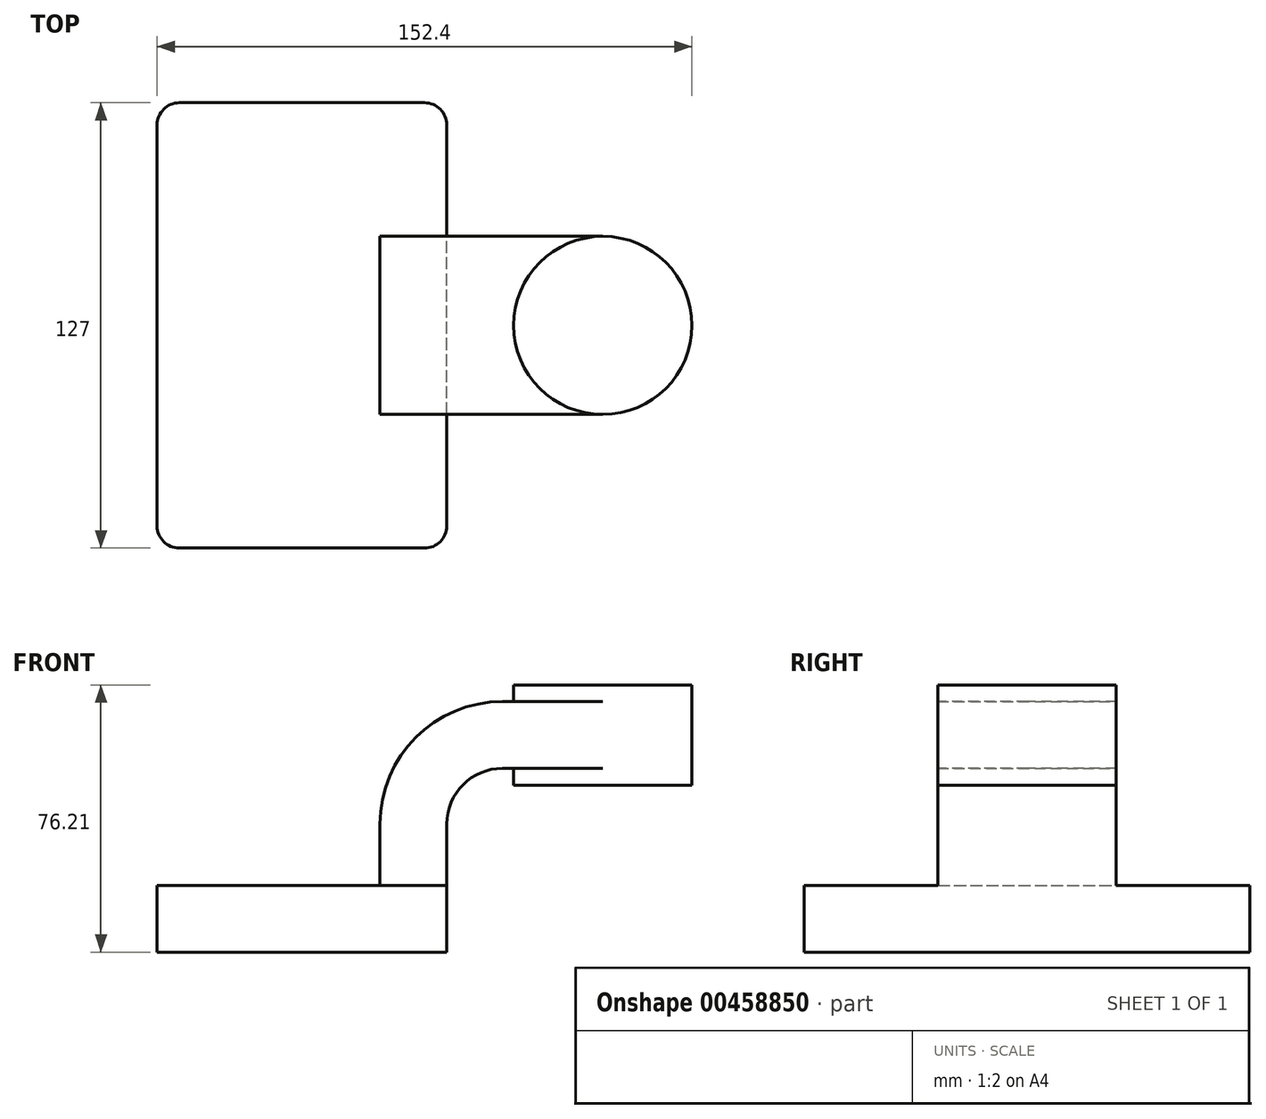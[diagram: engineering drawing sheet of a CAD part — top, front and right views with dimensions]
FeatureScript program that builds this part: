
annotation { "Feature Type Name" : "Feature", "Feature Type Description" : "" }
export const myFeature = defineFeature(function(context is Context, id is Id, definition is map)
    precondition{}
    {
        {
            var Q0;
            Q0=qCreatedBy(makeId("Front.planeOp"),FACE);
            var sketch = newSketch(context, id + "F0", { "sketchPlane" : qUnion([Q0])});
            skLineSegment(sketch, "E0.bottom", {"start": v(41.28, -9.52) * mm, "end": v(-41.28, -9.53) * mm});
            skLineSegment(sketch, "E0.top", {"start": v(41.27, 9.53) * mm, "end": v(-41.28, 9.53) * mm});
            skLineSegment(sketch, "E0.left", {"start": v(41.28, -9.52) * mm, "end": v(41.28, 9.53) * mm});
            skLineSegment(sketch, "E0.right", {"start": v(-41.28, -9.53) * mm, "end": v(-41.28, 9.53) * mm});
            skPoint(sketch, "E0.middle", {"position": v(0, 0) * mm});
            skLineSegment(sketch, "E1.bottom", {"start": v(60.33, 38.1) * mm, "end": v(111.13, 38.1) * mm});
            skLineSegment(sketch, "E1.top", {"start": v(60.32, 66.68) * mm, "end": v(111.13, 66.68) * mm});
            skLineSegment(sketch, "E1.left", {"start": v(60.33, 38.1) * mm, "end": v(60.32, 66.68) * mm});
            skLineSegment(sketch, "E1.right", {"start": v(111.13, 38.1) * mm, "end": v(111.12, 66.68) * mm});
            skPoint(sketch, "E1.middle", {"position": v(85.72, 52.39) * mm});
            skLineSegment(sketch, "E2", {"start": v(41.27, 9.53) * mm, "end": v(41.27, 27) * mm});
            skArc(sketch, "E3", {"start": v(41.27, 27) * mm, "mid": v(45.92, 38.23) * mm, "end": v(57.15, 42.88) * mm});
            skLineSegment(sketch, "E4", {"start": v(57.15, 42.88) * mm, "end": v(85.73, 42.88) * mm});
            skPoint(sketch, "E5.endSnap0", {"position": v(85.73, 66.68) * mm});
            skLineSegment(sketch, "E6.0", {"start": v(57.15, 61.93) * mm, "end": v(85.76, 61.93) * mm});
            skArc(sketch, "E6.1", {"start": v(22.23, 27) * mm, "mid": v(32.45, 51.7) * mm, "end": v(57.15, 61.93) * mm});
            skLineSegment(sketch, "E6.2", {"start": v(22.22, 9.53) * mm, "end": v(22.22, 27) * mm});
            skLineSegment(sketch, "E7", {"start": v(85.73, 38.1) * mm, "end": v(85.73, 66.68) * mm});
            skFitSpline(sketch, "E8", {"points": [v(-41.28, 9.52) * mm, v(57.15, 61.93) * mm], "startDerivative": vector(40.9, 81.24) * mm, "endDerivative": vector(129.26, -13.52) * mm});
            skSolve(sketch);
        }
        {
            var Q0;
            Q0=makeQuery(id+"F0.imprint","IMPRINT",FACE,{"disambiguationData":[TD([[makeQuery(id+"F0.imprint","IMPRINT",EDGE,{"derivedFrom":sQuery(id+"F0.wireOp",EDGE,"E0.bottom")}),-1.0]])]});
            extrude(context, id + "F1", {"entities" : qUnion([Q0]), "depth" : 127 * mm, "symmetric" : true});
        }
        {
            var Q0;
            {var subQ1=sQuery(id+"F0.wireOp",EDGE,"E2");Q0=makeQuery(id+"F0.imprint","IMPRINT",FACE,{"disambiguationData":[TD([[makeQuery(id+"F0.imprint","IMPRINT",EDGE,{"derivedFrom":subQ1}),1.0]])]});}
            var Q1;
            {var subQ0=sQuery(id+"F0.wireOp",EDGE,"E4");var subQ1=sQuery(id+"F0.wireOp",EDGE,"E1.left");var subQ2=makeQuery(id+"F0.imprint","INTERSECT",VERTEX,{"derivedFrom":[subQ1,subQ0]});Q1=makeQuery(id+"F0.imprint","IMPRINT",FACE,{"disambiguationData":[TD([[makeQuery(id+"F0.imprint","IMPRINT",EDGE,{"disambiguationData":[TD([[subQ2,-1.0]])],"derivedFrom":subQ1}),-1.0]])]});}
            extrude(context, id + "F2", {"entities" : qUnion([Q0, Q1]), "operationType" : NewBodyOperationType.ADD, "depth" : 50.8 * mm, "symmetric" : true});
        }
        {
            var Q0;
            {var subQ0=sQuery(id+"F0.wireOp",EDGE,"E1.right");Q0=makeQuery(id+"F0.imprint","IMPRINT",FACE,{"disambiguationData":[TD([[makeQuery(id+"F0.imprint","IMPRINT",EDGE,{"derivedFrom":subQ0}),1.0]])]});}
            var Q1;
            Q1=sQuery(id+"F0.wireOp",EDGE,"E7");
            revolve(context, id + "F3", {"operationType" : NewBodyOperationType.ADD, "entities" : qUnion([Q0]), "axis" : qUnion([Q1]), "revolveType" : RevolveType.FULL});
        }
        {
            var Q0;
            Q0=makeQuery(id+"F0.imprint","IMPRINT",FACE,{"disambiguationData":[TD([[makeQuery(id+"F0.imprint","IMPRINT",EDGE,{"derivedFrom":sQuery(id+"F0.wireOp",EDGE,"E6.1")}),1.0]])]});
            extrude(context, id + "F4", {"entities" : qUnion([Q0]), "operationType" : NewBodyOperationType.ADD, "depth" : 15.88 * mm, "symmetric" : true});
        }
        {
            var Q0;
            Q0=makeQuery(id+"F1.opExtrude","CAP_EDGE",EDGE,{"disambiguationData":[OSD([sQuery(id+"F0.wireOp",EDGE,"E0.right")])],"isStart":true});
            var Q1;
            Q1=makeQuery(id+"F1.opExtrude","CAP_EDGE",EDGE,{"disambiguationData":[OSD([sQuery(id+"F0.wireOp",EDGE,"E0.right")])],"isStart":false});
            var Q2;
            Q2=makeQuery(id+"F1.opExtrude","CAP_EDGE",EDGE,{"disambiguationData":[OSD([sQuery(id+"F0.wireOp",EDGE,"E0.left")])],"isStart":false});
            var Q3;
            Q3=makeQuery(id+"F1.opExtrude","CAP_EDGE",EDGE,{"disambiguationData":[OSD([sQuery(id+"F0.wireOp",EDGE,"E0.left")])],"isStart":true});
            fillet(context, id + "F5", {"entities" : qUnion([Q0, Q1, Q2, Q3]), "radius" : 6.35 * mm, "tangentPropagation" : true, "allowEdgeOverflow" : false});
        }
    });
